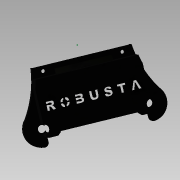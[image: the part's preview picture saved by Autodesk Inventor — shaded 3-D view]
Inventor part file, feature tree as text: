
AUTODESK INVENTOR PART (.ipt)
format: ipt  version: 2015 SP1 (Build 190203100, 203)  size: 775,680 bytes
history: native  units: mm
features: sketch x19, extrude x17, projected_geometry x9, fillet x5, plane x4
ambient origin geometry x8: Origin, YZ Plane, XZ Plane, XY Plane, X Axis, Y Axis, Z Axis, Center Point
bodies: Body1 (feature_tree)
feature tree (54):
  plane  "Work Plane2"
  sketch  "Sketch12"  dims[d19=46.65mm d72=0.0mm d125=-8.5mm d129=3.5mm]
  plane  "Work Plane3"
  extrude  "Extrusion9"  Depth=3.5mm
  extrude  "Extrusion10"  Depth=7.0mm TaperAngle=0.0deg
  extrude  "Extrusion11"  Depth=13.5mm TaperAngle=0.0deg
  extrude  "Extrusion12"  Depth=3.5mm TaperAngle=0.0deg
  extrude  "Extrusion13"  Depth=3.5mm TaperAngle=0.0deg
  extrude  "Extrusion14"  Depth=4.46mm
  extrude  "Extrusion15"  Depth=50.0mm TaperAngle=0.0deg
  plane  "Work Plane4"
  extrude  "Extrusion16"  Depth=7.1mm
  extrude  "Extrusion17"  Depth=7.1mm
  extrude  "Extrusion18"  Depth=7.1mm
  extrude  "Extrusion19"  Depth=8.0mm
  extrude  "Extrusion20"  TaperAngle=90.0deg  [1 undecoded]
  extrude  "Extrusion21"  Depth=80.0mm TaperAngle=0.0deg
  fillet  "Fillet1"  Radius=13.5mm
  extrude  "Extrusion22"  Depth=13.5mm TaperAngle=0.0deg
  fillet  "Fillet2"  Radius=4.0mm
  fillet  "Fillet3"  Radius=4.0mm
  fillet  "Fillet4"  Radius=4.0mm
  extrude  "Extrusion23"  Depth=1.0mm
  fillet  "Fillet5"  [1 undecoded]
  extrude  "Extrusion24"  Depth=2.0mm
  sketch  "Sketch34"  dims[d199=3.5mm d200=0.0mm d201=2.0mm]
  sketch  "Sketch35"  dims[d202=46.987914mm d203=12.02274mm]
  plane  "Work Plane5"
  sketch  "Sketch36"  dims[d204=3.5mm]
  extrude  "Extrusion25"  Depth=12.02274mm
  sketch  "Sketch13"  dims[d136=-5.0mm d137=7.0mm d138=0.0mm]
  sketch  "Sketch16"  dims[d139=3.5mm d140=0.0mm d143=13.5mm d144=0.0mm]
  projected_geometry  "Projected Loop1"
  projected_geometry  "Projected Loop2"
  projected_geometry  "Projected Loop3"
  sketch  "Sketch17"  dims[d145=3.5mm d146=0.0mm d147=3.5mm d148=0.0mm]
  sketch  "Sketch18"  dims[d149=3.5mm d150=0.0mm d158=3.5mm d159=0.0mm]
  projected_geometry  "Projected Loop4"
  sketch  "Sketch19"  dims[d161=0.0mm d162=4.46mm]
  projected_geometry  "Projected Loop6"
  sketch  "Sketch20"  dims[d163=45.0deg d164=50.0mm d165=0.0mm]
  sketch  "Sketch21"  dims[d166=7.1mm d167=7.1mm]
  sketch  "Sketch22"  dims[d168=0.0mm d169=0.0mm d170=7.1mm]
  sketch  "Sketch25"  dims[d171=50.0mm d172=0.0mm d173=7.1mm]
  sketch  "Sketch29"  dims[d174=50.0mm d175=0.0mm d178=8.0mm]
  sketch  "Sketch30"  dims[d180=11.0mm d182=90.0deg]
  projected_geometry  "Projected Loop14"
  sketch  "Sketch31"  dims[d183=0.5mm d186=80.0mm d187=0.0mm d188=13.5mm d189=0.0mm]
  sketch  "Sketch32"  dims[d190=4.0mm d191=13.5mm d192=0.0mm d193=4.0mm d194=4.0mm d195=4.0mm]
  projected_geometry  "Projected Loop15"
  projected_geometry  "Projected Loop16"
  sketch  "Sketch33"  dims[d196=1.0mm d197=1.0mm d198=0.0mm]
  projected_geometry  "Projected Loop17"
  sketch  "Sketch37"  dims[d205=3.5mm d206=0.0mm d207=-42.0mm d208=13.5mm d209=0.0mm]
note: 2 required parameter values undecoded (feature->parameter linkage not recoverable at this tier; creation-order binding heuristic only, values carry confidence <= 0.55)
